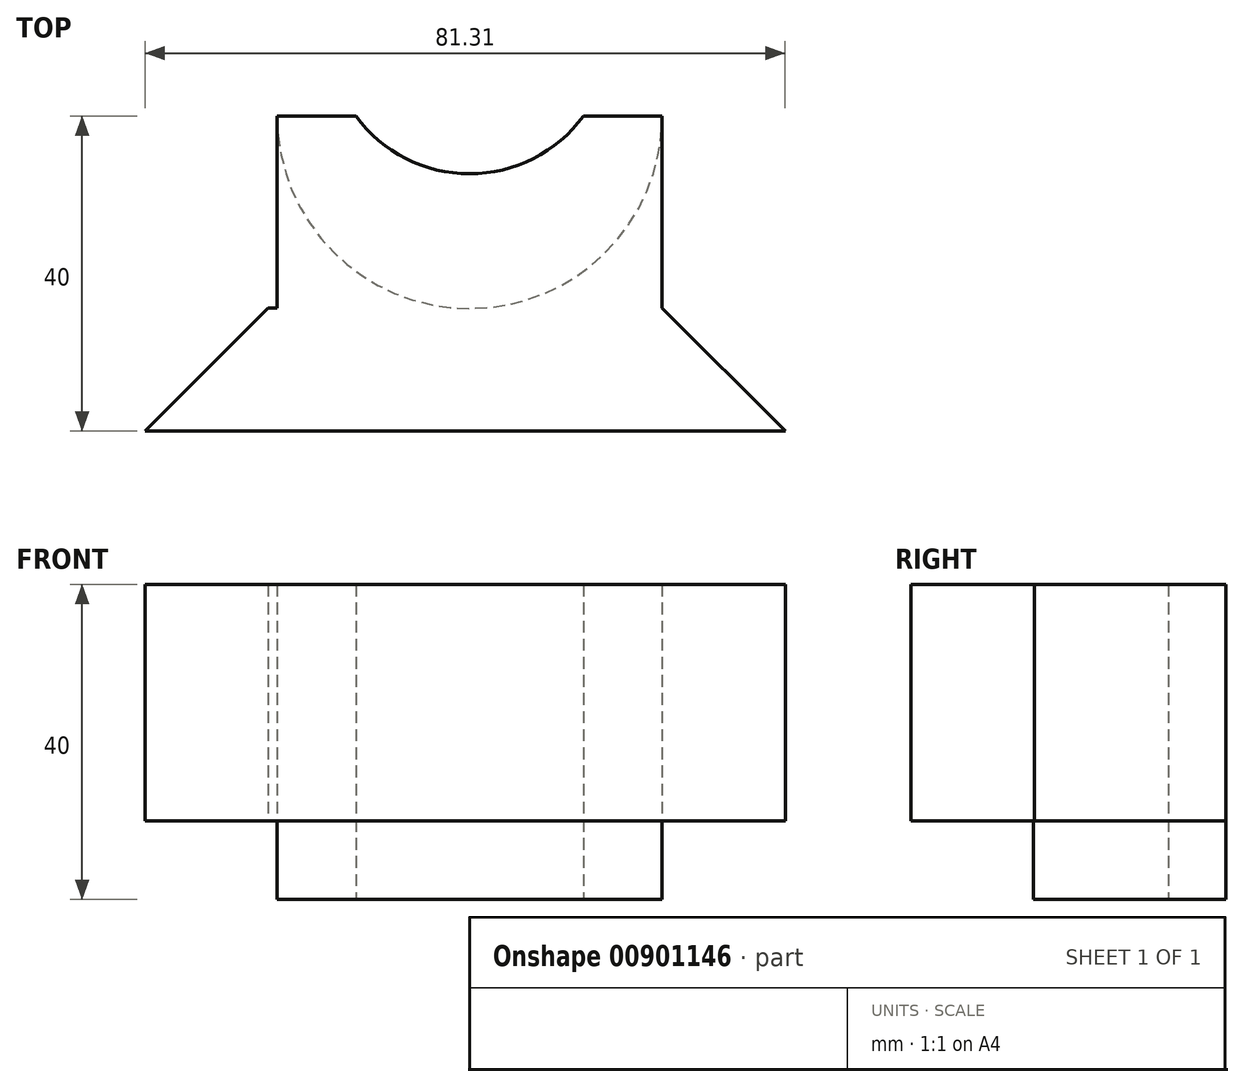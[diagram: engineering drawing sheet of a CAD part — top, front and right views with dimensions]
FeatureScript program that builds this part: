
annotation { "Feature Type Name" : "Feature", "Feature Type Description" : "" }
export const myFeature = defineFeature(function(context is Context, id is Id, definition is map)
    precondition{}
    {
        {
            var Q0;
            Q0=qCreatedBy(makeId("Top.planeOp"),FACE);
            var sketch = newSketch(context, id + "F0", { "sketchPlane" : qUnion([Q0])});
            skLineSegment(sketch, "E0", {"start": v(-35.88, -37.4) * mm, "end": v(44.12, -37.4) * mm});
            skLineSegment(sketch, "E1", {"start": v(-35.88, -37.4) * mm, "end": v(-20.24, -21.75) * mm});
            skLineSegment(sketch, "E2", {"start": v(45.43, -37.4) * mm, "end": v(29.8, -21.75) * mm});
            skLineSegment(sketch, "E3", {"start": v(44.12, -37.4) * mm, "end": v(45.43, -37.4) * mm});
            skPoint(sketch, "E4.start.orphan", {"position": v(-20.24, 2.6) * mm});
            skPoint(sketch, "E5.end.orphan", {"position": v(29.8, 2.6) * mm});
            skLineSegment(sketch, "E6", {"start": v(-20.24, -21.75) * mm, "end": v(-10.24, -21.75) * mm});
            skLineSegment(sketch, "E7", {"start": v(29.8, -21.75) * mm, "end": v(19.8, -21.75) * mm});
            skArc(sketch, "E8", {"start": v(-9.1, 2.6) * mm, "mid": v(5.34, -4.72) * mm, "end": v(19.8, 2.6) * mm});
            skArc(sketch, "E9", {"start": v(-9.1, 2.6) * mm, "mid": v(5.34, -11.84) * mm, "end": v(19.8, 2.6) * mm});
            skLineSegment(sketch, "E10", {"start": v(-9.1, 2.6) * mm, "end": v(-19.1, 2.6) * mm});
            skLineSegment(sketch, "E11", {"start": v(-19.1, 2.6) * mm, "end": v(-19.1, -21.75) * mm});
            skLineSegment(sketch, "E12", {"start": v(19.8, 2.6) * mm, "end": v(29.8, 2.6) * mm});
            skLineSegment(sketch, "E13", {"start": v(29.8, 2.6) * mm, "end": v(29.8, -21.75) * mm});
            skPoint(sketch, "E14.end.orphan", {"position": v(-9.1, -21.75) * mm});
            skSolve(sketch);
        }
        {
            var Q0;
            Q0 = qSketchRegion(id + "F0", true);
            extrude(context, id + "F1", {"entities" : qUnion([Q0]), "depth" : 30 * mm, "offsetDistance" : 25 * mm});
        }
        {
            var Q0;
            Q0=makeQuery(id+"F1.opExtrude","CAP_FACE",FACE,{"disambiguationData":[OSD([sQuery(id+"F0.wireOp",EDGE,"E0"),sQuery(id+"F0.wireOp",EDGE,"E1"),sQuery(id+"F0.wireOp",EDGE,"E2"),sQuery(id+"F0.wireOp",EDGE,"E3"),sQuery(id+"F0.wireOp",EDGE,"E6"),sQuery(id+"F0.wireOp",EDGE,"E7"),sQuery(id+"F0.wireOp",EDGE,"E8"),sQuery(id+"F0.wireOp",EDGE,"E10"),sQuery(id+"F0.wireOp",EDGE,"E11"),sQuery(id+"F0.wireOp",EDGE,"E12"),sQuery(id+"F0.wireOp",EDGE,"E13")])],"isStart":true});
            var sketch = newSketch(context, id + "F2", { "sketchPlane" : qUnion([Q0])});
            skArc(sketch, "E15", {"start": v(29.8, -2.6) * mm, "mid": v(5.34, 21.84) * mm, "end": v(-19.1, -2.6) * mm});
            skSolve(sketch);
        }
        {
            var Q0;
            Q0 = qSketchRegion(id + "F2", true);
            var Q1;
            Q1=makeQuery(id+"F2.imprint","IMPRINT",FACE,{"disambiguationData":[TD([[makeQuery(id+"F2.imprint","IMPRINT",EDGE,{"derivedFrom":sQuery(id+"F2.wireOp",EDGE,"E15")}),1.0]])]});
            extrude(context, id + "F3", {"entities" : qUnion([Q0, Q1]), "operationType" : NewBodyOperationType.ADD, "depth" : 10 * mm, "offsetDistance" : 25 * mm});
        }
    });
